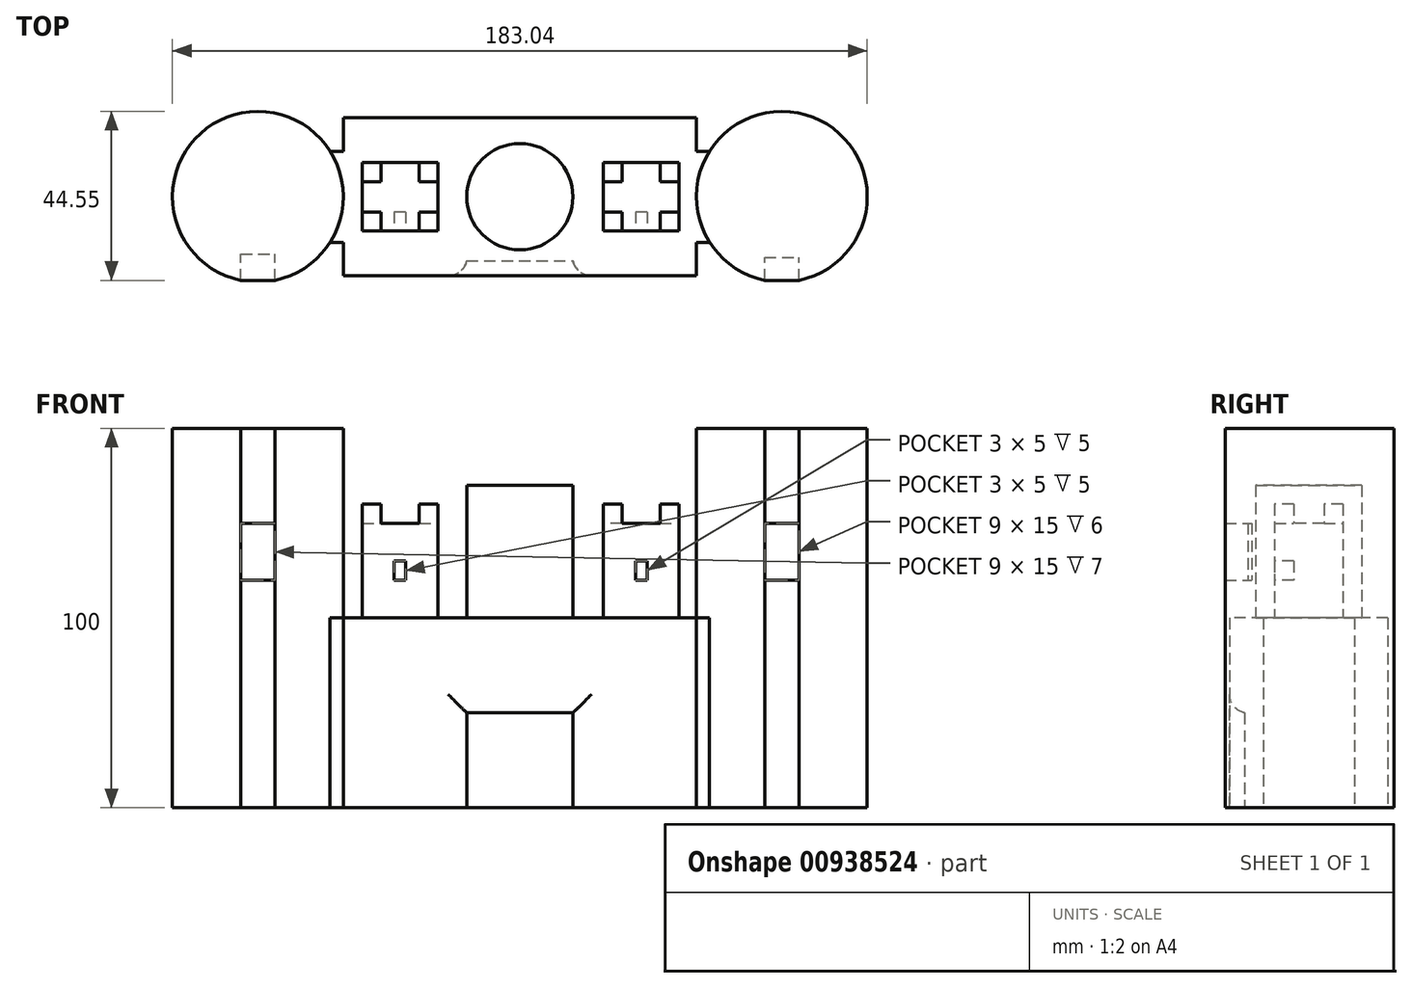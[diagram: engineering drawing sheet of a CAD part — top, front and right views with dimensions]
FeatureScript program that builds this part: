
annotation { "Feature Type Name" : "Feature", "Feature Type Description" : "" }
export const myFeature = defineFeature(function(context is Context, id is Id, definition is map)
    precondition{}
    {
        {
            var Q0;
            Q0=qCreatedBy(makeId("Top.planeOp"),FACE);
            var sketch = newSketch(context, id + "F0", { "sketchPlane" : qUnion([Q0])});
            skLineSegment(sketch, "E0.bottom", {"start": v(46.52, 20.86) * mm, "end": v(-46.52, 20.86) * mm});
            skLineSegment(sketch, "E0.top", {"start": v(46.52, -20.86) * mm, "end": v(-46.52, -20.86) * mm});
            skLineSegment(sketch, "E0.left", {"start": v(46.52, 20.86) * mm, "end": v(46.52, -20.86) * mm});
            skLineSegment(sketch, "E0.right", {"start": v(-46.52, 20.86) * mm, "end": v(-46.52, -20.86) * mm});
            skPoint(sketch, "E0.middle", {"position": v(0, 0) * mm});
            skCircle(sketch, "E1", {"center": v(69.02, 0) * mm, "radius": 22.5 * mm});
            skCircle(sketch, "E2", {"center": v(-69.02, 0) * mm, "radius": 22.5 * mm});
            skLineSegment(sketch, "E3.bottom", {"start": v(-21.52, 9) * mm, "end": v(-41.52, 9) * mm});
            skLineSegment(sketch, "E3.top", {"start": v(-21.52, -9) * mm, "end": v(-41.52, -9) * mm});
            skLineSegment(sketch, "E3.left", {"start": v(-21.52, 9) * mm, "end": v(-21.52, -9) * mm});
            skLineSegment(sketch, "E3.right", {"start": v(-41.52, 9) * mm, "end": v(-41.52, -9) * mm});
            skPoint(sketch, "E3.middle", {"position": v(-31.52, 0) * mm});
            skLineSegment(sketch, "E4.bottom", {"start": v(41.94, 9) * mm, "end": v(21.94, 9) * mm});
            skLineSegment(sketch, "E4.top", {"start": v(41.94, -9) * mm, "end": v(21.94, -9) * mm});
            skLineSegment(sketch, "E4.left", {"start": v(41.94, 9) * mm, "end": v(41.94, -9) * mm});
            skLineSegment(sketch, "E4.right", {"start": v(21.94, 9) * mm, "end": v(21.94, -9) * mm});
            skCircle(sketch, "E5", {"center": v(0, 0) * mm, "radius": 14 * mm});
            skLineSegment(sketch, "E6.bottom", {"start": v(36.94, 4) * mm, "end": v(41.94, 4) * mm});
            skLineSegment(sketch, "E6.top", {"start": v(36.94, 9) * mm, "end": v(41.94, 9) * mm});
            skLineSegment(sketch, "E6.left", {"start": v(36.94, 4) * mm, "end": v(36.94, 9) * mm});
            skLineSegment(sketch, "E6.right", {"start": v(41.94, 4) * mm, "end": v(41.94, 9) * mm});
            skPoint(sketch, "E6.middle", {"position": v(39.44, 6.5) * mm});
            skLineSegment(sketch, "E7.bottom", {"start": v(36.94, -9) * mm, "end": v(41.94, -9) * mm});
            skLineSegment(sketch, "E7.top", {"start": v(36.94, -4) * mm, "end": v(41.94, -4) * mm});
            skLineSegment(sketch, "E7.left", {"start": v(36.94, -9) * mm, "end": v(36.94, -4) * mm});
            skLineSegment(sketch, "E7.right", {"start": v(41.94, -9) * mm, "end": v(41.94, -4) * mm});
            skPoint(sketch, "E7.middle", {"position": v(39.44, -6.5) * mm});
            skLineSegment(sketch, "E8.bottom", {"start": v(26.94, -9) * mm, "end": v(21.94, -9) * mm});
            skLineSegment(sketch, "E8.top", {"start": v(26.94, -4) * mm, "end": v(21.94, -4) * mm});
            skLineSegment(sketch, "E8.left", {"start": v(26.94, -9) * mm, "end": v(26.94, -4) * mm});
            skLineSegment(sketch, "E8.right", {"start": v(21.94, -9) * mm, "end": v(21.94, -4) * mm});
            skPoint(sketch, "E8.middle", {"position": v(24.44, -6.5) * mm});
            skLineSegment(sketch, "E9.bottom", {"start": v(-26.52, 4) * mm, "end": v(-21.52, 4) * mm});
            skLineSegment(sketch, "E9.top", {"start": v(-26.52, 9) * mm, "end": v(-21.52, 9) * mm});
            skLineSegment(sketch, "E9.left", {"start": v(-26.52, 4) * mm, "end": v(-26.52, 9) * mm});
            skLineSegment(sketch, "E9.right", {"start": v(-21.52, 4) * mm, "end": v(-21.52, 9) * mm});
            skPoint(sketch, "E9.middle", {"position": v(-24.02, 6.5) * mm});
            skLineSegment(sketch, "E10.bottom", {"start": v(-26.52, -9) * mm, "end": v(-21.52, -9) * mm});
            skLineSegment(sketch, "E10.top", {"start": v(-26.52, -4) * mm, "end": v(-21.52, -4) * mm});
            skLineSegment(sketch, "E10.left", {"start": v(-26.52, -9) * mm, "end": v(-26.52, -4) * mm});
            skLineSegment(sketch, "E10.right", {"start": v(-21.52, -9) * mm, "end": v(-21.52, -4) * mm});
            skPoint(sketch, "E10.middle", {"position": v(-24.02, -6.5) * mm});
            skLineSegment(sketch, "E11.bottom", {"start": v(-41.52, 4) * mm, "end": v(-36.52, 4) * mm});
            skLineSegment(sketch, "E11.top", {"start": v(-41.52, 9) * mm, "end": v(-36.52, 9) * mm});
            skLineSegment(sketch, "E11.left", {"start": v(-41.52, 4) * mm, "end": v(-41.52, 9) * mm});
            skLineSegment(sketch, "E11.right", {"start": v(-36.52, 4) * mm, "end": v(-36.52, 9) * mm});
            skPoint(sketch, "E11.middle", {"position": v(-39.02, 6.5) * mm});
            skLineSegment(sketch, "E12.bottom", {"start": v(-36.52, -9) * mm, "end": v(-41.52, -9) * mm});
            skLineSegment(sketch, "E12.top", {"start": v(-36.52, -4) * mm, "end": v(-41.52, -4) * mm});
            skLineSegment(sketch, "E12.left", {"start": v(-36.52, -9) * mm, "end": v(-36.52, -4) * mm});
            skLineSegment(sketch, "E12.right", {"start": v(-41.52, -9) * mm, "end": v(-41.52, -4) * mm});
            skPoint(sketch, "E12.middle", {"position": v(-39.02, -6.5) * mm});
            skLineSegment(sketch, "E13", {"start": v(-49.98, 12) * mm, "end": v(-46.52, 12) * mm});
            skLineSegment(sketch, "E14", {"start": v(-49.98, -12) * mm, "end": v(-46.52, -12) * mm});
            skLineSegment(sketch, "E15", {"start": v(21.94, 9) * mm, "end": v(26.94, 9) * mm});
            skLineSegment(sketch, "E16", {"start": v(26.94, 9) * mm, "end": v(26.94, 4) * mm});
            skLineSegment(sketch, "E17", {"start": v(26.94, 4) * mm, "end": v(21.94, 4) * mm});
            skLineSegment(sketch, "E18", {"start": v(21.94, 4) * mm, "end": v(21.94, 9) * mm});
            skLineSegment(sketch, "E19", {"start": v(46.52, -12) * mm, "end": v(49.98, -12) * mm});
            skLineSegment(sketch, "E20", {"start": v(46.52, 12) * mm, "end": v(49.98, 12) * mm});
            skLineSegment(sketch, "E21.bottom", {"start": v(-14, -20.86) * mm, "end": v(14, -20.86) * mm});
            skLineSegment(sketch, "E21.top", {"start": v(-14, -16.88) * mm, "end": v(14, -16.88) * mm});
            skLineSegment(sketch, "E21.left", {"start": v(-14, -20.86) * mm, "end": v(-14, -16.88) * mm});
            skLineSegment(sketch, "E21.right", {"start": v(14, -20.86) * mm, "end": v(14, -16.88) * mm});
            skLineSegment(sketch, "E22.bottom", {"start": v(-73.52, -22.05) * mm, "end": v(-64.52, -22.05) * mm});
            skLineSegment(sketch, "E22.top", {"start": v(-73.52, -15.05) * mm, "end": v(-64.52, -15.05) * mm});
            skLineSegment(sketch, "E22.left", {"start": v(-73.52, -22.05) * mm, "end": v(-73.52, -15.05) * mm});
            skLineSegment(sketch, "E22.right", {"start": v(-64.52, -22.05) * mm, "end": v(-64.52, -15.05) * mm});
            skLineSegment(sketch, "E23.bottom", {"start": v(64.52, -22.05) * mm, "end": v(73.52, -22.05) * mm});
            skLineSegment(sketch, "E23.top", {"start": v(64.52, -16.05) * mm, "end": v(73.52, -16.05) * mm});
            skLineSegment(sketch, "E23.left", {"start": v(64.52, -22.05) * mm, "end": v(64.52, -16.05) * mm});
            skLineSegment(sketch, "E23.right", {"start": v(73.52, -22.05) * mm, "end": v(73.52, -16.05) * mm});
            skPoint(sketch, "E24.middle.positionSnap0", {"position": v(-31.52, -9) * mm});
            skPoint(sketch, "E24.centerSnap0", {"position": v(-31.52, -9) * mm});
            skLineSegment(sketch, "E25.bottom", {"start": v(-30.1, -4) * mm, "end": v(-33.1, -4) * mm});
            skLineSegment(sketch, "E25.top", {"start": v(-30.1, -9) * mm, "end": v(-33.1, -9) * mm});
            skLineSegment(sketch, "E25.left", {"start": v(-30.1, -4) * mm, "end": v(-30.1, -9) * mm});
            skLineSegment(sketch, "E25.right", {"start": v(-33.1, -4) * mm, "end": v(-33.1, -9) * mm});
            skPoint(sketch, "E25.middle", {"position": v(-31.6, -6.5) * mm});
            skLineSegment(sketch, "E26.bottom", {"start": v(33.53, -4) * mm, "end": v(30.53, -4) * mm});
            skLineSegment(sketch, "E26.top", {"start": v(33.53, -9) * mm, "end": v(30.53, -9) * mm});
            skLineSegment(sketch, "E26.left", {"start": v(33.53, -4) * mm, "end": v(33.53, -9) * mm});
            skLineSegment(sketch, "E26.right", {"start": v(30.53, -4) * mm, "end": v(30.53, -9) * mm});
            skPoint(sketch, "E26.middle", {"position": v(32.03, -6.5) * mm});
            skSolve(sketch);
        }
        {
            var Q0;
            Q0=makeQuery(id+"F0.imprint","IMPRINT",FACE,{"disambiguationData":[TD([[makeQuery(id+"F0.imprint","IMPRINT",EDGE,{"derivedFrom":sQuery(id+"F0.wireOp",EDGE,"E22.top")}),1.0]])]});
            var Q1;
            Q1=makeQuery(id+"F0.imprint","IMPRINT",FACE,{"disambiguationData":[TD([[makeQuery(id+"F0.imprint","IMPRINT",EDGE,{"derivedFrom":sQuery(id+"F0.wireOp",EDGE,"E23.top")}),1.0]])]});
            extrude(context, id + "F1", {"entities" : qUnion([Q0, Q1]), "depth" : 100 * mm, "offsetDistance" : 25 * mm});
        }
        {
            var Q0;
            {var subQ30=sQuery(id+"F0.wireOp",EDGE,"E0.bottom");Q0=makeQuery(id+"F0.imprint","IMPRINT",FACE,{"disambiguationData":[TD([[makeQuery(id+"F0.imprint","IMPRINT",EDGE,{"derivedFrom":subQ30}),1.0]])]});}
            var Q1;
            {var subQ0=sQuery(id+"F0.wireOp",EDGE,"E14");Q1=makeQuery(id+"F0.imprint","IMPRINT",FACE,{"disambiguationData":[TD([[makeQuery(id+"F0.imprint","IMPRINT",EDGE,{"derivedFrom":subQ0}),1.0]])]});}
            var Q2;
            {var subQ0=sQuery(id+"F0.wireOp",EDGE,"E13");Q2=makeQuery(id+"F0.imprint","IMPRINT",FACE,{"disambiguationData":[TD([[makeQuery(id+"F0.imprint","IMPRINT",EDGE,{"derivedFrom":subQ0}),-1.0]])]});}
            var Q3;
            {var subQ3=sQuery(id+"F0.wireOp",EDGE,"E19");Q3=makeQuery(id+"F0.imprint","IMPRINT",FACE,{"disambiguationData":[TD([[makeQuery(id+"F0.imprint","IMPRINT",EDGE,{"derivedFrom":subQ3}),1.0]])]});}
            var Q4;
            {var subQ3=sQuery(id+"F0.wireOp",EDGE,"E20");Q4=makeQuery(id+"F0.imprint","IMPRINT",FACE,{"disambiguationData":[TD([[makeQuery(id+"F0.imprint","IMPRINT",EDGE,{"derivedFrom":subQ3}),-1.0]])]});}
            extrude(context, id + "F2", {"entities" : qUnion([Q0, Q1, Q2, Q3, Q4]), "operationType" : NewBodyOperationType.ADD, "depth" : 50 * mm, "offsetDistance" : 25 * mm});
        }
        {
            var Q0;
            {var subQ1=sQuery(id+"F0.wireOp",EDGE,"E6.bottom");Q0=makeQuery(id+"F0.imprint","IMPRINT",FACE,{"disambiguationData":[TD([[makeQuery(id+"F0.imprint","IMPRINT",EDGE,{"derivedFrom":subQ1}),-1.0]])]});}
            var Q1;
            {var subQ2=sQuery(id+"F0.wireOp",EDGE,"E9.bottom");Q1=makeQuery(id+"F0.imprint","IMPRINT",FACE,{"disambiguationData":[TD([[makeQuery(id+"F0.imprint","IMPRINT",EDGE,{"derivedFrom":subQ2}),-1.0]])]});}
            extrude(context, id + "F3", {"entities" : qUnion([Q0, Q1]), "depth" : 75 * mm, "offsetDistance" : 25 * mm});
        }
        {
            var Q0;
            Q0=makeQuery(id+"F0.imprint","IMPRINT",FACE,{"disambiguationData":[TD([[makeQuery(id+"F0.imprint","IMPRINT",EDGE,{"derivedFrom":sQuery(id+"F0.wireOp",EDGE,"E5")}),1.0]])]});
            extrude(context, id + "F4", {"entities" : qUnion([Q0]), "operationType" : NewBodyOperationType.ADD, "depth" : 85 * mm, "offsetDistance" : 25 * mm});
        }
        {
            var Q0;
            {var subQ4=sQuery(id+"F0.wireOp",EDGE,"E11.bottom");Q0=makeQuery(id+"F0.imprint","IMPRINT",FACE,{"disambiguationData":[TD([[makeQuery(id+"F0.imprint","IMPRINT",EDGE,{"derivedFrom":subQ4}),1.0]])]});}
            var Q1;
            {var subQ4=sQuery(id+"F0.wireOp",EDGE,"E12.top");Q1=makeQuery(id+"F0.imprint","IMPRINT",FACE,{"disambiguationData":[TD([[makeQuery(id+"F0.imprint","IMPRINT",EDGE,{"derivedFrom":subQ4}),1.0]])]});}
            var Q2;
            {var subQ4=sQuery(id+"F0.wireOp",EDGE,"E10.top");Q2=makeQuery(id+"F0.imprint","IMPRINT",FACE,{"disambiguationData":[TD([[makeQuery(id+"F0.imprint","IMPRINT",EDGE,{"derivedFrom":subQ4}),-1.0]])]});}
            var Q3;
            {var subQ4=sQuery(id+"F0.wireOp",EDGE,"E9.bottom");Q3=makeQuery(id+"F0.imprint","IMPRINT",FACE,{"disambiguationData":[TD([[makeQuery(id+"F0.imprint","IMPRINT",EDGE,{"derivedFrom":subQ4}),1.0]])]});}
            var Q4;
            Q4=makeQuery(id+"F0.imprint","IMPRINT",FACE,{"disambiguationData":[TD([[makeQuery(id+"F0.imprint","IMPRINT",EDGE,{"derivedFrom":sQuery(id+"F0.wireOp",EDGE,"MELGteSH-f8X1-jqJS-Ewsp-kI7gSk52piws.bottom")}),-1.0]])]});
            var Q5;
            {var subQ4=sQuery(id+"F0.wireOp",EDGE,"E8.top");Q5=makeQuery(id+"F0.imprint","IMPRINT",FACE,{"disambiguationData":[TD([[makeQuery(id+"F0.imprint","IMPRINT",EDGE,{"derivedFrom":subQ4}),1.0]])]});}
            var Q6;
            {var subQ4=sQuery(id+"F0.wireOp",EDGE,"E7.top");Q6=makeQuery(id+"F0.imprint","IMPRINT",FACE,{"disambiguationData":[TD([[makeQuery(id+"F0.imprint","IMPRINT",EDGE,{"derivedFrom":subQ4}),-1.0]])]});}
            var Q7;
            {var subQ4=sQuery(id+"F0.wireOp",EDGE,"E6.bottom");Q7=makeQuery(id+"F0.imprint","IMPRINT",FACE,{"disambiguationData":[TD([[makeQuery(id+"F0.imprint","IMPRINT",EDGE,{"derivedFrom":subQ4}),1.0]])]});}
            var Q8;
            {var subQ3=sQuery(id+"F0.wireOp",EDGE,"E16");Q8=makeQuery(id+"F0.imprint","IMPRINT",FACE,{"disambiguationData":[TD([[makeQuery(id+"F0.imprint","IMPRINT",EDGE,{"derivedFrom":subQ3}),-1.0]])]});}
            extrude(context, id + "F5", {"entities" : qUnion([Q0, Q1, Q2, Q3, Q4, Q5, Q6, Q7, Q8]), "operationType" : NewBodyOperationType.ADD, "depth" : 80 * mm, "offsetDistance" : 25 * mm});
        }
        {
            var Q0;
            Q0=makeQuery(id+"F0.imprint","IMPRINT",FACE,{"disambiguationData":[TD([[makeQuery(id+"F0.imprint","IMPRINT",EDGE,{"derivedFrom":sQuery(id+"F0.wireOp",EDGE,"E21.top")}),-1.0]])]});
            extrude(context, id + "F6", {"entities" : qUnion([Q0]), "operationType" : NewBodyOperationType.ADD, "depth" : 50 * mm, "offsetDistance" : 25 * mm, "hasSecondDirection" : true, "secondDirectionOppositeDirection" : false, "secondDirectionDepth" : 25 * mm});
        }
        {
            var Q0;
            Q0=makeQuery(id+"F0.imprint","IMPRINT",FACE,{"disambiguationData":[TD([[makeQuery(id+"F0.imprint","IMPRINT",EDGE,{"derivedFrom":sQuery(id+"F0.wireOp",EDGE,"E22.bottom")}),1.0]])]});
            var Q1;
            Q1=makeQuery(id+"F0.imprint","IMPRINT",FACE,{"disambiguationData":[TD([[makeQuery(id+"F0.imprint","IMPRINT",EDGE,{"derivedFrom":sQuery(id+"F0.wireOp",EDGE,"E23.bottom")}),1.0]])]});
            extrude(context, id + "F7", {"entities" : qUnion([Q0, Q1]), "operationType" : NewBodyOperationType.ADD, "depth" : 100 * mm, "offsetDistance" : 25 * mm, "hasSecondDirection" : true, "secondDirectionOppositeDirection" : false, "secondDirectionDepth" : 75 * mm});
        }
        {
            var Q0;
            Q0=makeQuery(id+"F0.imprint","IMPRINT",FACE,{"disambiguationData":[TD([[makeQuery(id+"F0.imprint","IMPRINT",EDGE,{"derivedFrom":sQuery(id+"F0.wireOp",EDGE,"E22.bottom")}),1.0]])]});
            var Q1;
            Q1=makeQuery(id+"F0.imprint","IMPRINT",FACE,{"disambiguationData":[TD([[makeQuery(id+"F0.imprint","IMPRINT",EDGE,{"derivedFrom":sQuery(id+"F0.wireOp",EDGE,"E23.bottom")}),1.0]])]});
            extrude(context, id + "F8", {"entities" : qUnion([Q0, Q1]), "operationType" : NewBodyOperationType.ADD, "depth" : 60 * mm, "offsetDistance" : 25 * mm});
        }
        {
            var Q0;
            Q0=makeQuery(id+"F6.opExtrude","CAP_EDGE",EDGE,{"disambiguationData":[OSD([sQuery(id+"F0.wireOp",EDGE,"E0.top")])],"isStart":true});
            var Q1;
            Q1=makeQuery(id+"F2.opExtrude","SWEPT_EDGE",EDGE,{"disambiguationData":[OSD([sQuery(id+"F0.wireOp",EDGE,"E0.top"),sQuery(id+"F0.wireOp",EDGE,"E21.left")])]});
            var Q2;
            Q2=makeQuery(id+"F2.opExtrude","SWEPT_EDGE",EDGE,{"disambiguationData":[OSD([sQuery(id+"F0.wireOp",EDGE,"E0.top"),sQuery(id+"F0.wireOp",EDGE,"E21.right")])]});
            fillet(context, id + "F9", {"entities" : qUnion([Q0, Q1, Q2]), "radius" : 5 * mm, "tangentPropagation" : true, "allowEdgeOverflow" : false});
        }
        {
            var Q0;
            Q0=makeQuery(id+"F0.imprint","IMPRINT",FACE,{"disambiguationData":[TD([[makeQuery(id+"F0.imprint","IMPRINT",EDGE,{"derivedFrom":sQuery(id+"F0.wireOp",EDGE,"E25.bottom")}),1.0]])]});
            var Q1;
            Q1=makeQuery(id+"F0.imprint","IMPRINT",FACE,{"disambiguationData":[TD([[makeQuery(id+"F0.imprint","IMPRINT",EDGE,{"derivedFrom":sQuery(id+"F0.wireOp",EDGE,"E26.bottom")}),1.0]])]});
            extrude(context, id + "F10", {"entities" : qUnion([Q0, Q1]), "operationType" : NewBodyOperationType.ADD, "depth" : 75 * mm, "offsetDistance" : 25 * mm, "hasSecondDirection" : true, "secondDirectionOppositeDirection" : false, "secondDirectionDepth" : 65 * mm});
        }
        {
            var Q0;
            Q0=makeQuery(id+"F0.imprint","IMPRINT",FACE,{"disambiguationData":[TD([[makeQuery(id+"F0.imprint","IMPRINT",EDGE,{"derivedFrom":sQuery(id+"F0.wireOp",EDGE,"E25.bottom")}),1.0]])]});
            var Q1;
            Q1=makeQuery(id+"F0.imprint","IMPRINT",FACE,{"disambiguationData":[TD([[makeQuery(id+"F0.imprint","IMPRINT",EDGE,{"derivedFrom":sQuery(id+"F0.wireOp",EDGE,"E26.bottom")}),1.0]])]});
            extrude(context, id + "F11", {"entities" : qUnion([Q0, Q1]), "operationType" : NewBodyOperationType.ADD, "depth" : 60 * mm, "offsetDistance" : 25 * mm});
        }
    });
